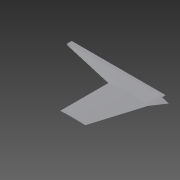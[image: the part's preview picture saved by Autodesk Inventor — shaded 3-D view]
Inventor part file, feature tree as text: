
AUTODESK INVENTOR PART (.ipt)
format: ipt  version: 2014 SP1 (Build 180222100, 222)  size: 193,536 bytes
history: native  units: mm
features: sketch x4, plane x3, loft x2, extrude x1, fillet x1, other x1
ambient origin geometry x8: Origin, YZ Plane, XZ Plane, XY Plane, X Axis, Y Axis, Z Axis, Center Point
bodies: Solid1 (feature_tree)
feature tree (12):
  sketch  "Sketch1"  dims[d0=490.0mm d11=60.0mm]
  plane  "Work Plane1"
  sketch  "Sketch2"  dims[d12=230.0mm d13=120.0mm]
  plane  "Work Plane2"
  loft  "Loft1"
  loft  "Loft2"
  plane  "Work Plane3"
  extrude  "Extrusion2"  TaperAngle=0.0deg  [1 undecoded]
  fillet  "Fillet1"  [1 undecoded]
  sketch  "Sketch3"  dims[d14=0.0mm d15=90.0deg d16=0.0mm d17=90.0deg d18=0.0mm d19=90.0deg]
  other  "Edges1"
  sketch  "Sketch4"  dims[d20=0.0mm d21=90.0deg d22=0.0mm d23=450.0mm d24=2.5mm d25=450.0mm d26=5.0mm d27=450.0mm d28=25.0mm d29=0.0mm d30=40.0mm]
note: 2 required parameter values undecoded (feature->parameter linkage not recoverable at this tier; creation-order binding heuristic only, values carry confidence <= 0.55)
